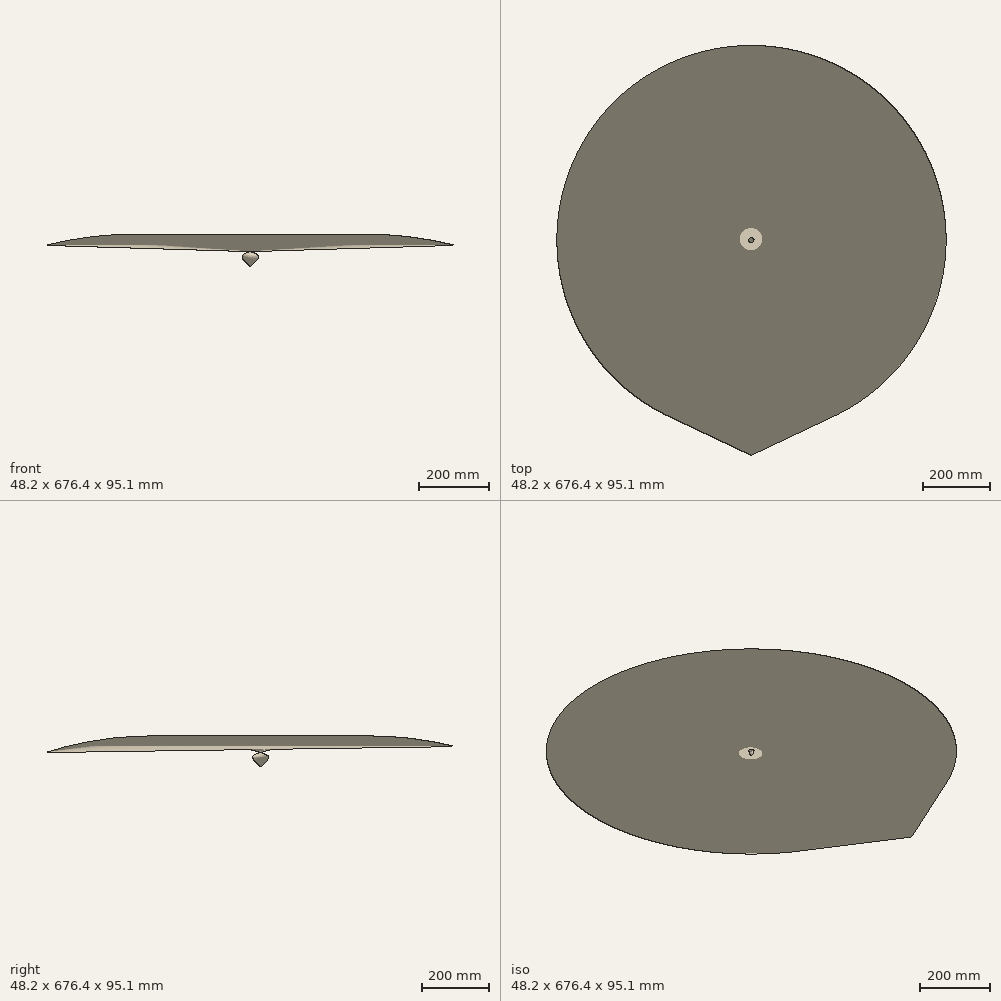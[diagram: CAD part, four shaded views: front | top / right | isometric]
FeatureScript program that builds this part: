
annotation { "Feature Type Name" : "Feature", "Feature Type Description" : "" }
export const myFeature = defineFeature(function(context is Context, id is Id, definition is map)
    precondition{}
    {
        {
            var Q0;
            Q0=qCreatedBy(makeId("Right.planeOp"),FACE);
            var sketch = newSketch(context, id + "F0", { "sketchPlane" : qUnion([Q0])});
            skLineSegment(sketch, "E0", {"start": v(0, 0) * mm, "end": v(0, 64.25) * mm});
            skArc(sketch, "E1", {"start": v(0, 64.25) * mm, "mid": v(-15.68, 54.14) * mm, "end": v(0, 44.03) * mm});
            skFitSpline(sketch, "E2", {"points": [v(0, 44.03) * mm, v(-23.99, 30.32) * mm, v(0, 0) * mm], "startDerivative": vector(-74.5, -23.96) * mm, "endDerivative": vector(70.44, -63.01) * mm});
            skSolve(sketch);
        }
        {
            var Q0;
            {var subQ0=sQuery(id+"F0.wireOp",EDGE,"E2");var subQ1=sQuery(id+"F0.wireOp",EDGE,"E0");var subQ2=makeQuery(id+"F0.imprint","INTERSECT",VERTEX,{"derivedFrom":[subQ1,subQ0]});Q0=makeQuery(id+"F0.imprint","IMPRINT",FACE,{"disambiguationData":[TD([[makeQuery(id+"F0.imprint","IMPRINT",EDGE,{"disambiguationData":[TD([[subQ2,1.0]])],"derivedFrom":subQ0}),1.0]])]});}
            var Q1;
            {var subQ0=sQuery(id+"F0.wireOp",EDGE,"E1");var subQ1=sQuery(id+"F0.wireOp",EDGE,"E0");var subQ2=makeQuery(id+"F0.imprint","INTERSECT",VERTEX,{"derivedFrom":[subQ1,subQ0]});Q1=makeQuery(id+"F0.imprint","IMPRINT",FACE,{"disambiguationData":[TD([[makeQuery(id+"F0.imprint","IMPRINT",EDGE,{"disambiguationData":[TD([[subQ2,-1.0]])],"derivedFrom":subQ0}),1.0]])]});}
            var Q2;
            Q2=sQuery(id+"F0.wireOp",EDGE,"E0");
            revolve(context, id + "F1", {"entities" : qUnion([Q0, Q1]), "axis" : qUnion([Q2]), "revolveType" : RevolveType.FULL});
        }
        {
            var Q0;
            Q0=qCreatedBy(makeId("Top.planeOp"),FACE);
            var sketch = newSketch(context, id + "F2", { "sketchPlane" : qUnion([Q0])});
            skCircle(sketch, "E3", {"center": v(0, 0) * mm, "radius": 5.85 * mm});
            skSolve(sketch);
        }
        {
            var Q0;
            Q0 = qSketchRegion(id + "F2", true);
            extrude(context, id + "F3", {"entities" : qUnion([Q0]), "operationType" : NewBodyOperationType.REMOVE, "oppositeDirection" : true, "depth" : 25.4 * mm});
        }
    });
